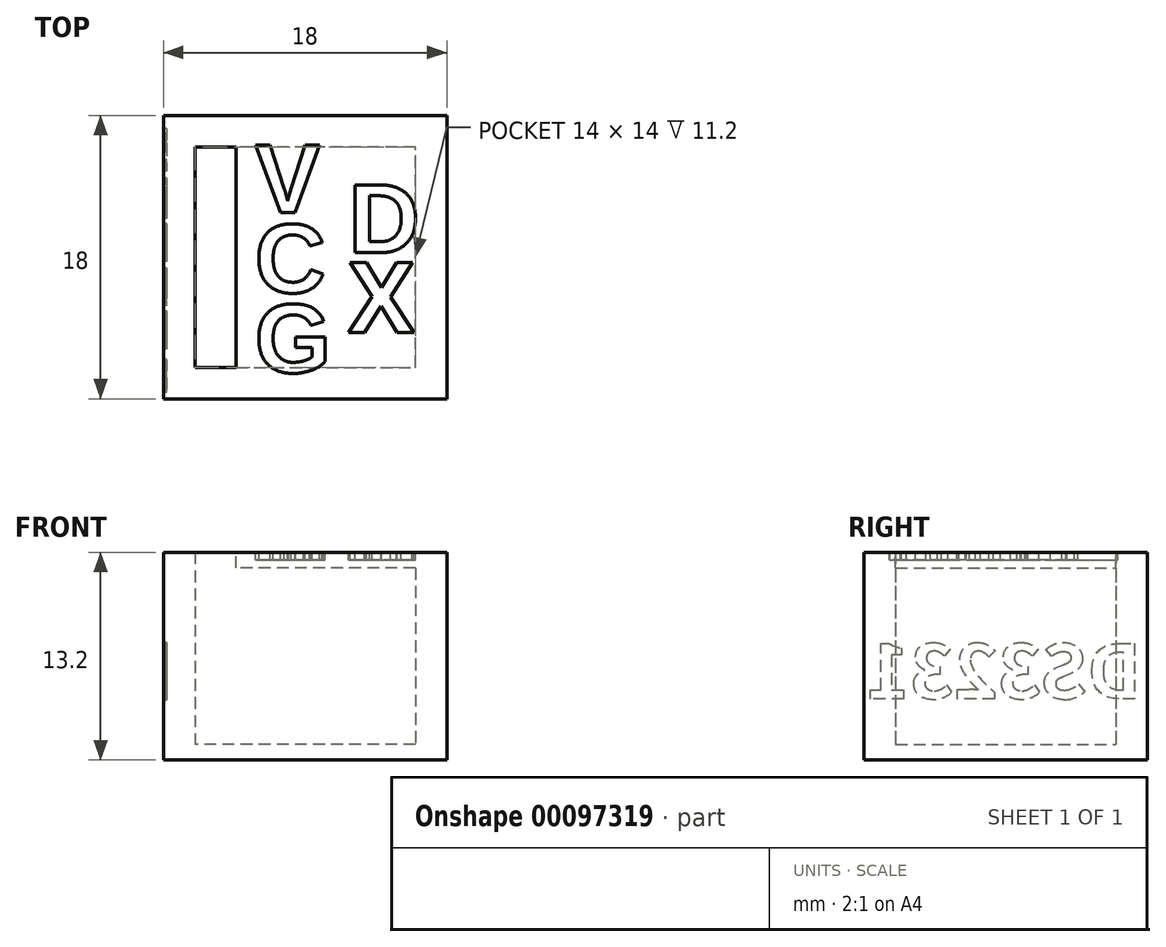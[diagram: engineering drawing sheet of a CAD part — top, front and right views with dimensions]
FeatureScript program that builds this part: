
annotation { "Feature Type Name" : "Feature", "Feature Type Description" : "" }
export const myFeature = defineFeature(function(context is Context, id is Id, definition is map)
    precondition{}
    {
        {
            var Q0;
            Q0=qCreatedBy(makeId("Top.planeOp"),FACE);
            var sketch = newSketch(context, id + "F0", { "sketchPlane" : qUnion([Q0])});
            skLineSegment(sketch, "E0.bottom", {"start": v(-7, 7) * mm, "end": v(7, 7) * mm});
            skLineSegment(sketch, "E0.top", {"start": v(-7, -7) * mm, "end": v(7, -7) * mm});
            skLineSegment(sketch, "E0.left", {"start": v(-7, 7) * mm, "end": v(-7, -7) * mm});
            skLineSegment(sketch, "E0.right", {"start": v(7, 7) * mm, "end": v(7, -7) * mm});
            skPoint(sketch, "E0.middle", {"position": v(0, 0) * mm});
            skLineSegment(sketch, "E1.0", {"start": v(-8, 8) * mm, "end": v(8, 8) * mm});
            skLineSegment(sketch, "E1.1", {"start": v(-8, 8) * mm, "end": v(-8, -8) * mm});
            skLineSegment(sketch, "E1.2", {"start": v(-8, -8) * mm, "end": v(8, -8) * mm});
            skLineSegment(sketch, "E1.3", {"start": v(8, 8) * mm, "end": v(8, -8) * mm});
            skLineSegment(sketch, "E2.0", {"start": v(-9, 9) * mm, "end": v(9, 9) * mm});
            skLineSegment(sketch, "E2.1", {"start": v(-9, 9) * mm, "end": v(-9, -9) * mm});
            skLineSegment(sketch, "E2.2", {"start": v(-9, -9) * mm, "end": v(9, -9) * mm});
            skLineSegment(sketch, "E2.3", {"start": v(9, 9) * mm, "end": v(9, -9) * mm});
            skSolve(sketch);
        }
        {
            var Q0;
            Q0=makeQuery(id+"F0.imprint","IMPRINT",FACE,{"disambiguationData":[TD([[makeQuery(id+"F0.imprint","IMPRINT",EDGE,{"derivedFrom":sQuery(id+"F0.wireOp",EDGE,"E1.0")}),1.0]])]});
            var Q1;
            Q1=makeQuery(id+"F0.imprint","IMPRINT",FACE,{"disambiguationData":[TD([[makeQuery(id+"F0.imprint","IMPRINT",EDGE,{"derivedFrom":sQuery(id+"F0.wireOp",EDGE,"E0.bottom")}),1.0]])]});
            var Q2;
            Q2=makeQuery(id+"F0.imprint","IMPRINT",FACE,{"disambiguationData":[TD([[makeQuery(id+"F0.imprint","IMPRINT",EDGE,{"derivedFrom":sQuery(id+"F0.wireOp",EDGE,"E0.bottom")}),-1.0]])]});
            extrude(context, id + "F1", {"entities" : qUnion([Q0, Q1, Q2]), "depth" : 1 * mm});
        }
        {
            var Q0;
            Q0=makeQuery(id+"F0.imprint","IMPRINT",FACE,{"disambiguationData":[TD([[makeQuery(id+"F0.imprint","IMPRINT",EDGE,{"derivedFrom":sQuery(id+"F0.wireOp",EDGE,"E0.bottom")}),1.0]])]});
            extrude(context, id + "F2", {"entities" : qUnion([Q0]), "operationType" : NewBodyOperationType.ADD, "depth" : 10.2 * mm});
        }
        {
            var Q0;
            Q0=makeQuery(id+"F0.imprint","IMPRINT",FACE,{"disambiguationData":[TD([[makeQuery(id+"F0.imprint","IMPRINT",EDGE,{"derivedFrom":sQuery(id+"F0.wireOp",EDGE,"E1.0")}),1.0]])]});
            extrude(context, id + "F3", {"entities" : qUnion([Q0]), "operationType" : NewBodyOperationType.ADD, "depth" : 11.2 * mm});
        }
        {
            var Q0;
            Q0=qCreatedBy(makeId("Top.planeOp"),FACE);
            cPlane(context, id + "F4", {"entities" : qUnion([Q0]), "cplaneType" : CPlaneType.OFFSET, "offset" : 13.2 * mm, "width" : 150 * mm, "height" : 150 * mm});
        }
        {
            var Q0;
            Q0=qCreatedBy(id+"F4.planeOp",FACE);
            var sketch = newSketch(context, id + "F5", { "sketchPlane" : qUnion([Q0])});
            skLineSegment(sketch, "E3.0.0", {"start": v(-7, 7) * mm, "end": v(-7, -7) * mm});
            skLineSegment(sketch, "E3.0.1", {"start": v(-7, -7) * mm, "end": v(7, -7) * mm});
            skLineSegment(sketch, "E3.0.2", {"start": v(7, -7) * mm, "end": v(7, 7) * mm});
            skLineSegment(sketch, "E3.0.3", {"start": v(7, 7) * mm, "end": v(-7, 7) * mm});
            skLineSegment(sketch, "E4.0.0", {"start": v(8, 8) * mm, "end": v(-8, 8) * mm});
            skLineSegment(sketch, "E4.0.1", {"start": v(-8, 8) * mm, "end": v(-8, -8) * mm});
            skLineSegment(sketch, "E4.0.2", {"start": v(-8, -8) * mm, "end": v(8, -8) * mm});
            skLineSegment(sketch, "E4.0.3", {"start": v(8, -8) * mm, "end": v(8, 8) * mm});
            skLineSegment(sketch, "E5.0", {"start": v(9, 9) * mm, "end": v(9, -9) * mm});
            skLineSegment(sketch, "E6.0.0", {"start": v(9, 9) * mm, "end": v(-9, 9) * mm});
            skLineSegment(sketch, "E6.0.1", {"start": v(-9, 9) * mm, "end": v(-9, -9) * mm});
            skLineSegment(sketch, "E6.0.2", {"start": v(-9, -9) * mm, "end": v(9, -9) * mm});
            skLineSegment(sketch, "E6.0.3", {"start": v(9, -9) * mm, "end": v(9, 9) * mm});
            skLineSegment(sketch, "E7", {"start": v(-4.4, 7) * mm, "end": v(-4.4, -7) * mm});
            skSolve(sketch);
        }
        {
            var Q0;
            Q0=makeQuery(id+"F5.imprint","IMPRINT",FACE,{"disambiguationData":[TD([[makeQuery(id+"F5.imprint","IMPRINT",EDGE,{"derivedFrom":sQuery(id+"F5.wireOp",EDGE,"E3.0.0")}),-1.0]])]});
            var Q1;
            Q1=makeQuery(id+"F5.imprint","IMPRINT",FACE,{"disambiguationData":[TD([[makeQuery(id+"F5.imprint","IMPRINT",EDGE,{"derivedFrom":sQuery(id+"F5.wireOp",EDGE,"E4.0.0")}),-1.0]])]});
            var Q2;
            {var subQ0=sQuery(id+"F5.wireOp",EDGE,"E3.0.2");Q2=makeQuery(id+"F5.imprint","IMPRINT",FACE,{"disambiguationData":[TD([[makeQuery(id+"F5.imprint","IMPRINT",EDGE,{"derivedFrom":subQ0}),1.0]])]});}
            extrude(context, id + "F6", {"entities" : qUnion([Q0, Q1, Q2]), "oppositeDirection" : true, "depth" : 1 * mm});
        }
        {
            var Q0;
            Q0=makeQuery(id+"F5.imprint","IMPRINT",FACE,{"disambiguationData":[TD([[makeQuery(id+"F5.imprint","IMPRINT",EDGE,{"derivedFrom":sQuery(id+"F5.wireOp",EDGE,"E3.0.0")}),-1.0]])]});
            extrude(context, id + "F7", {"entities" : qUnion([Q0]), "operationType" : NewBodyOperationType.ADD, "oppositeDirection" : true, "depth" : 3 * mm});
        }
        {
            var Q0;
            Q0=makeQuery(id+"F5.imprint","IMPRINT",FACE,{"disambiguationData":[TD([[makeQuery(id+"F5.imprint","IMPRINT",EDGE,{"derivedFrom":sQuery(id+"F5.wireOp",EDGE,"E4.0.0")}),-1.0]])]});
            extrude(context, id + "F8", {"entities" : qUnion([Q0]), "operationType" : NewBodyOperationType.ADD, "oppositeDirection" : true, "depth" : 2 * mm});
        }
        {
            var Q0;
            {var subQ0=sQuery(id+"F5.wireOp",EDGE,"E3.0.2");Q0=makeQuery(id+"F5.imprint","IMPRINT",FACE,{"disambiguationData":[TD([[makeQuery(id+"F5.imprint","IMPRINT",EDGE,{"derivedFrom":subQ0}),1.0]])]});}
            var sketch = newSketch(context, id + "F9", { "sketchPlane" : qUnion([Q0])});
            skLineSegment(sketch, "E8.0", {"start": v(-4.4, 7) * mm, "end": v(-7, 7) * mm});
            skLineSegment(sketch, "E9.0", {"start": v(-4.4, 7) * mm, "end": v(-4.4, -7) * mm});
            skLineSegment(sketch, "E10", {"start": v(-4.4, 5.08) * mm, "end": v(3.19, 5.08) * mm, "construction": true});
            skLineSegment(sketch, "E11", {"start": v(-4.4, 2.54) * mm, "end": v(3.37, 2.54) * mm, "construction": true});
            skLineSegment(sketch, "E12", {"start": v(-4.4, 0) * mm, "end": v(3.17, 0) * mm, "construction": true});
            skPoint(sketch, "E12.endSnap0", {"position": v(-4.4, 0) * mm});
            skLineSegment(sketch, "E13", {"start": v(-4.4, -2.54) * mm, "end": v(3.04, -2.54) * mm, "construction": true});
            skLineSegment(sketch, "E14", {"start": v(-4.4, -5.08) * mm, "end": v(2.49, -5.08) * mm, "construction": true});
            skText(sketch, "E15", { "text": "V", "fontName": "Arimo-Bold.ttf"});
            skPoint(sketch, "E16", {"position": v(-3.2, 5.08) * mm});
            skText(sketch, "E17", { "text": "D\n", "fontName": "Arimo-Bold.ttf"});
            skPoint(sketch, "E18", {"position": v(2.76, 2.54) * mm});
            skText(sketch, "E19", { "text": "C\n", "fontName": "Arimo-Bold.ttf"});
            skPoint(sketch, "E20", {"position": v(-3.2, 0) * mm});
            skText(sketch, "E21", { "text": "G", "fontName": "Arimo-Bold.ttf"});
            skPoint(sketch, "E22", {"position": v(-3.2, -5.08) * mm});
            skText(sketch, "E23", { "text": "X", "fontName": "OpenSans-Bold.ttf"});
            skPoint(sketch, "E24", {"position": v(2.76, -2.54) * mm});
            skPoint(sketch, "E25.orphan", {"position": v(7, 7) * mm});
            const initialGuessF9  = {"E15": [-0.0032, 0.00283, 1, 0, 0.0045], "E17": [0.00276, 0.00029, 1, 0, 0.0045], "E19": [-0.0032, -0.00225, 1, 0, 0.0045], "E21": [-0.0032, -0.00733, 1, 0, 0.0045], "E23": [0.00276, -0.0048, 1, 0, 0.0045]};
            skSetInitialGuess(sketch, initialGuessF9);
            skSolve(sketch);
        }
        {
            var Q0;
            Q0 = qSketchRegion(id + "F9", true);
            extrude(context, id + "F10", {"entities" : qUnion([Q0]), "operationType" : NewBodyOperationType.REMOVE, "oppositeDirection" : true, "depth" : 0.5 * mm});
        }
        {
            var Q0;
            {var subQ0=sQuery(id+"F0.wireOp",EDGE,"E2.1");Q0=makeQuery(id+"F3.boolean.opBoolean","MERGE",FACE,{"derivedFrom":[makeQuery(id+"F1.opExtrude","SWEPT_FACE",FACE,{"disambiguationData":[OSD([subQ0])]}),makeQuery(id+"F3.opExtrude","SWEPT_FACE",FACE,{"disambiguationData":[OSD([subQ0])]})]});}
            var sketch = newSketch(context, id + "F11", { "sketchPlane" : qUnion([Q0])});
            skLineSegment(sketch, "E26", {"start": v(-9, 0) * mm, "end": v(9, 11.2) * mm, "construction": true});
            skPoint(sketch, "E27", {"position": v(0, 5.6) * mm});
            skText(sketch, "E28", { "text": "DS3231", "fontName": "NotoSansCJKsc-Bold.otf"});
            skPoint(sketch, "E29", {"position": v(-8.6, 5.6) * mm});
            const initialGuessF11  = {"E28": [-0.0086, 0.0039, 1, 0, 0.00341]};
            skSetInitialGuess(sketch, initialGuessF11);
            skSolve(sketch);
        }
        {
            var Q0;
            Q0 = qSketchRegion(id + "F11", true);
            extrude(context, id + "F12", {"entities" : qUnion([Q0]), "operationType" : NewBodyOperationType.REMOVE, "oppositeDirection" : true, "depth" : 0.2 * mm});
        }
    });
